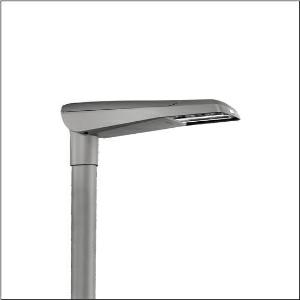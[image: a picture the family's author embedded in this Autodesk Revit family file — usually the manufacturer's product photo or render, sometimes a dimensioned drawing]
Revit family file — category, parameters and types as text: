
# Revit family: streetlight_sl_11_iq_micro___p1_0a_5xc1c41e08ce_7fd7
name_source: partatom
category: Lighting Fixtures
units: mm (PartAtom-declared; Revit-internal decimal feet)

## family parameters
Cut with Voids When Loaded = No
Host = Face
Light Source = No
Part Type = Normal
Room Calculation Point = No
Round Connector Dimension = Use Diameter
Shared = No

## types (1)
- --- (1 x LED, 1660 lm, 10.8 W, 4000K)
    Apparent Load = 11 VA
    CIE Flux Codes = 29 63 93 100 100
    Color Rendering = 70
    Color Temperature = 4000K
    Default Elevation = 1800 mm
    Description = Streetlight SL 11 iQ micro, mast luminaire, primary light control with 3 zone facetted reflector, of plastic, silver coated, highly specular, primary optical cover: cover, of PMMA, transparent, light distribution: P1.0a, light emission: direct distribution, primary light characteristic: asymmetric, installation type: post-top, side-entry, lamps: LED, High Power LED, rated values: 1.660lm | 10,8W | 153,7lm/W (begin service life); end service life: 1.660lm | 11,1W; at 50% lumin. flux: 830lm | 6W | 138,3lm/W, colour temperature: 4000K, colour rendering: CRI > 70, light colour: 740, light setting 1 begin service life: 100% | 1.660lm | 10,8W | 153,7lm/W | 4.000K, light setting 1 end service life: 11,1W, further light settings possible, control: optimised constant luminous flux control (CLO 2.0), Desk-Remote (wireless, voltage-free reading and setting of iQ features in the workshop via application-optimized NFC function/RFID function), Light-Fading, Smart-Wire, Night-Set, Lumen-Switch, Temp-Guard, Auto-Match, with cable H07RN-F 5x 1.5mm², mains connection: 230..240V, AC, 50/60Hz, connection cable pre-assembled, cable length: 5,5m, luminaire housing, of diecast aluminium, powder-coated, Siteco® metallic grey (DB 702S), please order mast flange separately, inclination adjustable without tools: 0°, 5°, 10°, 15° (post-top) | 0°, -5°, -10°, -15° (side-entry), sealing non-destructively replaceable, multi-level sealing system, length: 600mm, width: 174mm, height: 116mm, mast flange for spigot size: 42mm (side-entry): 5XC10008XM4, 60/48mm (side-entry/post-top): 5XC10108XM2, 76/60mm (side-entry/post-top): 5XC10108XM1, equipment: standard, protection rating (complete): IP66, insulation class (complete): insulation class II (safety insulation), certification: CE, ENEC, ENEC+, VDE, impact resistance: IK10, permissible operating ambient temperature for outdoor applications: -25..+50°C, standard-compliant lighting for roads and squares, Environmental Product Declaration (EPD) tested and certified by an independent institute, packaging unit: 1 piece

Light Distribution: P1.0a
    Height = 116 mm
    Lamp = 1 x LED
    Lamp Light Flux = 1660 lm
    Lamp Power = 10.8 W
    Lamp count = 1
    Length = 600 mm
    Luminous efficacy = 154 lm/W
    Manufacturer = Siteco
    ModVariant = No
    Model = 5XC1C41E08CE
    Number of Poles = 1
    OnlyDefault = Yes
    Power Factor = 1
    Product Name = Streetlight SL 11 iQ micro | P1.0a
    Product group = mast luminaire | pylon top
    ProductGroupID = 6100
    Protection Class = Protection class II
    Protection Degree = IP 66
    RLX_Detail_Level = 1
    RLX_Emergency_Light_Flux = 0 lm
    RLX_Emergency_Type = 0
    RLX_Emergency_Type_DB = No
    RlxData = <blob elided: 26645 chars, md5=6bfedf00>
    Socket = socket
    Standby Power = 0 W
    System Light Flux = 1660 lm
    System Power = 11 W
    Type Comments = factory setting: luminous flux: 100 % | dim-lin: 254 | 194 mA
    Type Image = l_1006566.jpg
    URL = http://relux.com
    VarID = @adj_018883
    Voltage = 0 V
    Weight = 0.00 kg
    Width = 174 mm

## geometry (parser evidence)
native form markers: Blend x4, Sweep x10
no freeform markers — native parametric forms only
